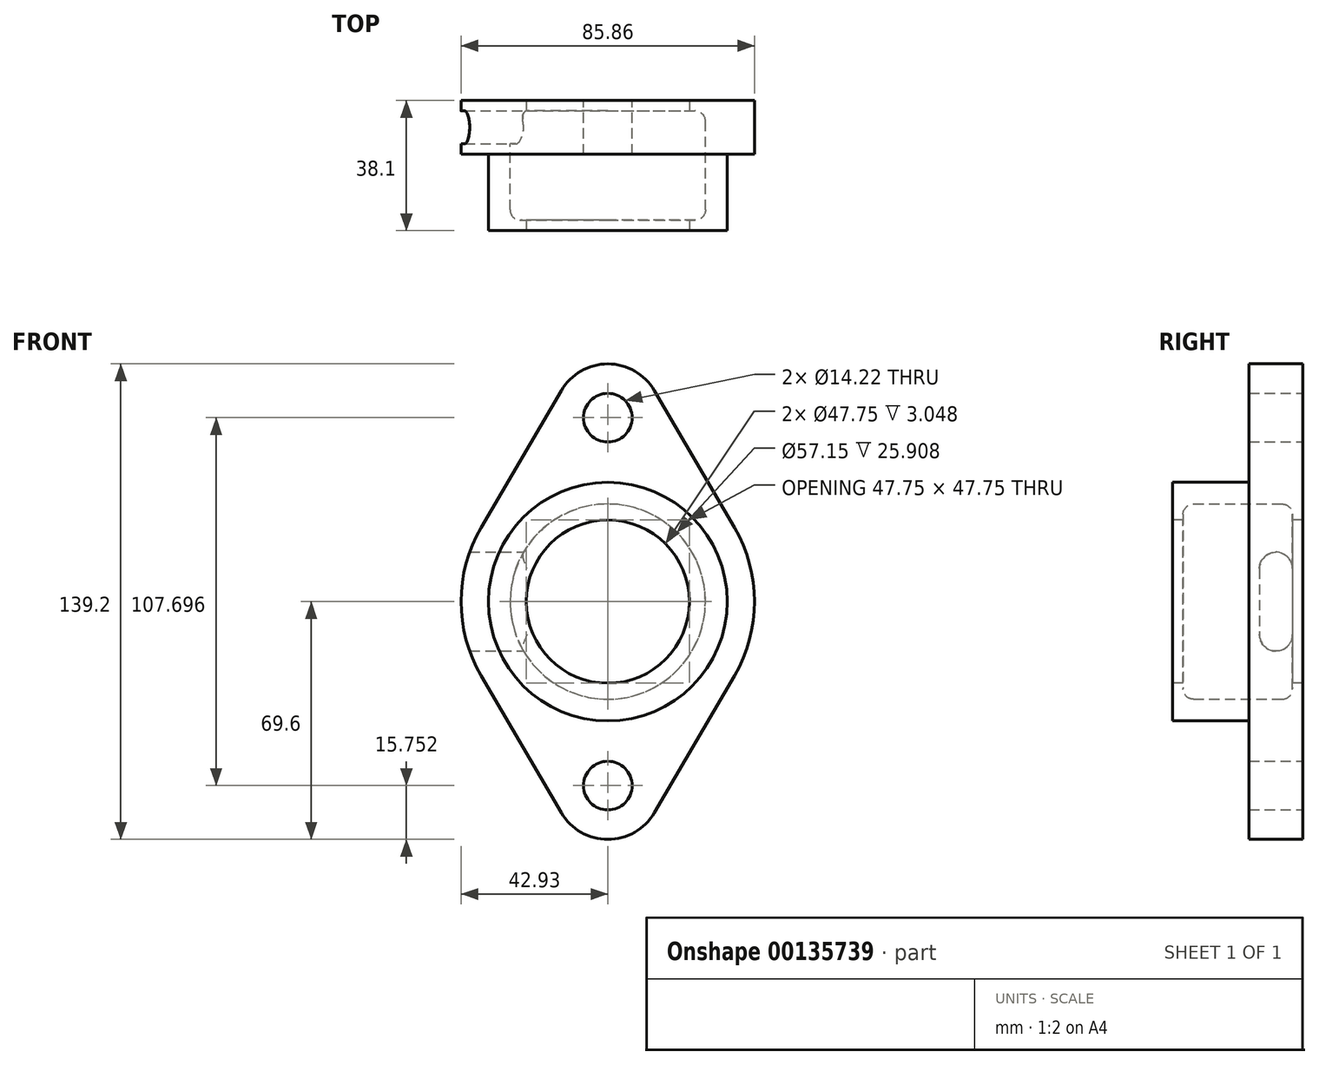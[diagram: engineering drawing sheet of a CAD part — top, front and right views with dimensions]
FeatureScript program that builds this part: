
annotation { "Feature Type Name" : "Feature", "Feature Type Description" : "" }
export const myFeature = defineFeature(function(context is Context, id is Id, definition is map)
    precondition{}
    {
        {
            var Q0;
            Q0=qCreatedBy(makeId("Front.planeOp"),FACE);
            var sketch = newSketch(context, id + "F0", { "sketchPlane" : qUnion([Q0])});
            skLineSegment(sketch, "E0", {"start": v(0, 53.85) * mm, "end": v(0, -53.85) * mm, "construction": true});
            skLineSegment(sketch, "E1", {"start": v(0, 0) * mm, "end": v(0, 0) * mm});
            skArc(sketch, "E2", {"start": v(-37.06, 21.67) * mm, "mid": v(-42.93, 0) * mm, "end": v(-37.06, -21.67) * mm});
            skLineSegment(sketch, "E3", {"start": v(-37.06, 21.67) * mm, "end": v(-13.6, 61.8) * mm});
            skArc(sketch, "E4", {"start": v(13.6, 61.8) * mm, "mid": v(0, 69.6) * mm, "end": v(-13.6, 61.8) * mm});
            skLineSegment(sketch, "E5", {"start": v(13.6, 61.8) * mm, "end": v(37.06, 21.67) * mm});
            skArc(sketch, "E6", {"start": v(37.06, -21.67) * mm, "mid": v(42.93, 0) * mm, "end": v(37.06, 21.67) * mm});
            skLineSegment(sketch, "E7", {"start": v(37.06, -21.67) * mm, "end": v(13.6, -61.8) * mm});
            skArc(sketch, "E8", {"start": v(-13.6, -61.8) * mm, "mid": v(0, -69.6) * mm, "end": v(13.6, -61.8) * mm});
            skLineSegment(sketch, "E9", {"start": v(-37.06, -21.67) * mm, "end": v(-13.6, -61.8) * mm});
            skCircle(sketch, "E10", {"center": v(0, 53.85) * mm, "radius": 7.11 * mm});
            skLineSegment(sketch, "E11", {"start": v(-13.67, 53.85) * mm, "end": v(14.35, 53.85) * mm, "construction": true});
            skLineSegment(sketch, "E12", {"start": v(-10.92, -53.85) * mm, "end": v(13.49, -53.85) * mm, "construction": true});
            skCircle(sketch, "E13", {"center": v(0, -53.85) * mm, "radius": 7.11 * mm});
            skSolve(sketch);
        }
        {
            var Q0;
            Q0=makeQuery(id+"F0.imprint","IMPRINT",FACE,{"disambiguationData":[TD([[makeQuery(id+"F0.imprint","IMPRINT",EDGE,{"derivedFrom":sQuery(id+"F0.wireOp",EDGE,"E2")}),1.0]])]});
            extrude(context, id + "F1", {"entities" : qUnion([Q0]), "depth" : 15.75 * mm});
        }
        {
            var Q0;
            Q0=makeQuery(id+"F1.opExtrude","CAP_FACE",FACE,{"disambiguationData":[OSD([sQuery(id+"F0.wireOp",EDGE,"E2"),sQuery(id+"F0.wireOp",EDGE,"E3"),sQuery(id+"F0.wireOp",EDGE,"E4"),sQuery(id+"F0.wireOp",EDGE,"E5"),sQuery(id+"F0.wireOp",EDGE,"E6"),sQuery(id+"F0.wireOp",EDGE,"E7"),sQuery(id+"F0.wireOp",EDGE,"E8"),sQuery(id+"F0.wireOp",EDGE,"E9"),sQuery(id+"F0.wireOp",EDGE,"E10"),sQuery(id+"F0.wireOp",EDGE,"E13")])],"isStart":false});
            var sketch = newSketch(context, id + "F2", { "sketchPlane" : qUnion([Q0])});
            skCircle(sketch, "E14", {"center": v(0, 0) * mm, "radius": 34.93 * mm});
            skSolve(sketch);
        }
        {
            var Q0;
            Q0=makeQuery(id+"F2.imprint","IMPRINT",FACE,{"disambiguationData":[TD([[makeQuery(id+"F2.imprint","IMPRINT",EDGE,{"derivedFrom":sQuery(id+"F2.wireOp",EDGE,"E14")}),1.0]])]});
            extrude(context, id + "F3", {"entities" : qUnion([Q0]), "operationType" : NewBodyOperationType.ADD, "depth" : 22.35 * mm});
        }
        {
            var Q0;
            Q0=qCreatedBy(makeId("Top.planeOp"),FACE);
            var sketch = newSketch(context, id + "F4", { "sketchPlane" : qUnion([Q0])});
            skLineSegment(sketch, "E15", {"start": v(0, 9.82) * mm, "end": v(0, -55.12) * mm, "construction": true});
            skLineSegment(sketch, "E16", {"start": v(0, -3.05) * mm, "end": v(-25.53, -3.05) * mm});
            skLineSegment(sketch, "E17", {"start": v(0, -3.05) * mm, "end": v(0, -35.05) * mm});
            skLineSegment(sketch, "E18", {"start": v(0, -35.05) * mm, "end": v(-25.53, -35.05) * mm});
            skArc(sketch, "E19", {"start": v(-25.53, -3.05) * mm, "mid": v(-27.68, -3.94) * mm, "end": v(-28.58, -6.1) * mm});
            skArc(sketch, "E20", {"start": v(-28.58, -32) * mm, "mid": v(-27.68, -34.16) * mm, "end": v(-25.53, -35.05) * mm});
            skLineSegment(sketch, "E21", {"start": v(-28.57, -6.1) * mm, "end": v(-28.57, -32) * mm});
            skLineSegment(sketch, "E22", {"start": v(42.93, 0) * mm, "end": v(42.93, -15.75) * mm});
            skSolve(sketch);
        }
        {
            var Q0;
            Q0 = qSketchRegion(id + "F4", true);
            var Q1;
            Q1=sQuery(id+"F4.wireOp",EDGE,"E17");
            revolve(context, id + "F5", {"operationType" : NewBodyOperationType.REMOVE, "entities" : qUnion([Q0]), "axis" : qUnion([Q1]), "revolveType" : RevolveType.FULL});
        }
        {
            var Q0;
            Q0=makeQuery(id+"F3.opExtrude","CAP_FACE",FACE,{"disambiguationData":[OSD([sQuery(id+"F2.wireOp",EDGE,"E14")])],"isStart":false});
            var sketch = newSketch(context, id + "F6", { "sketchPlane" : qUnion([Q0])});
            skCircle(sketch, "E23", {"center": v(0, 0) * mm, "radius": 23.88 * mm});
            skSolve(sketch);
        }
        {
            var Q0;
            Q0 = qSketchRegion(id + "F6", true);
            extrude(context, id + "F7", {"entities" : qUnion([Q0]), "operationType" : NewBodyOperationType.REMOVE, "endBound" : BoundingType.THROUGH_ALL, "oppositeDirection" : true, "depth" : 25.4 * mm});
        }
        {
            var Q0;
            Q0=qCreatedBy(makeId("Right.planeOp"),FACE);
            var sketch = newSketch(context, id + "F8", { "sketchPlane" : qUnion([Q0])});
            skLineSegment(sketch, "E24", {"start": v(-3.05, 9.65) * mm, "end": v(-3.05, -9.65) * mm});
            skLineSegment(sketch, "E25", {"start": v(-12.7, 9.65) * mm, "end": v(-12.7, -9.65) * mm});
            skArc(sketch, "E26", {"start": v(-3.05, 9.65) * mm, "mid": v(-7.87, 14.48) * mm, "end": v(-12.7, 9.65) * mm});
            skArc(sketch, "E27", {"start": v(-12.7, -9.65) * mm, "mid": v(-7.87, -14.48) * mm, "end": v(-3.05, -9.65) * mm});
            skSolve(sketch);
        }
        {
            var Q0;
            Q0 = qSketchRegion(id + "F8", true);
            extrude(context, id + "F9", {"entities" : qUnion([Q0]), "operationType" : NewBodyOperationType.REMOVE, "endBound" : BoundingType.THROUGH_ALL, "oppositeDirection" : true, "depth" : 25.4 * mm});
        }
    });
